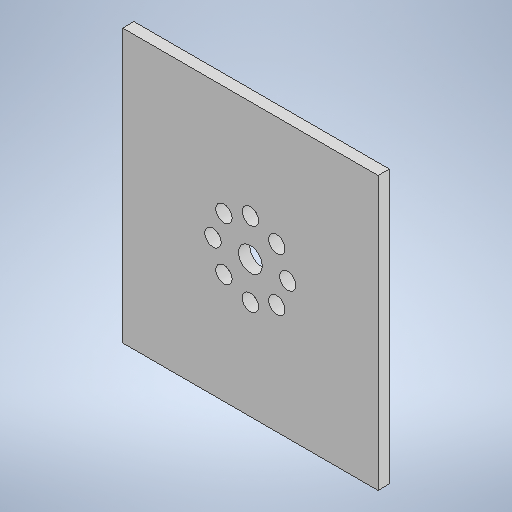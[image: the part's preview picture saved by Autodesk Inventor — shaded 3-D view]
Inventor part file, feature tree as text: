
AUTODESK INVENTOR PART (.ipt)
format: ipt  version: 2025.1 (Build 291241000, 241)  size: 232,448 bytes
history: native  units: mm
features: other x2, extrude x1, sketch x1
ambient origin geometry x8: Origin, YZ Plane, XZ Plane, XY Plane, X Axis, Y Axis, Z Axis, Center Point
bodies: Body1 (feature_tree)
feature tree (4):
  other  "ソリッド1"
  extrude  "押し出し1"  Depth=3.2mm
  sketch  "スケッチ1"
  other  "スケッチ円形状パターン1"
